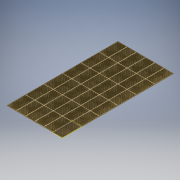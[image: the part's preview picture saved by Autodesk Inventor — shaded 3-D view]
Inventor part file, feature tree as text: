
AUTODESK INVENTOR PART (.ipt)
format: ipt  version: 2018 (Build 220112000, 112)  size: 17,295,360 bytes
history: native  units: in
note: dims shown in document units (in); Inventor stores cm internally (conversion verified against a paired STEP export)
features: extrude x2, sketch x2, plane x1, pattern_linear x1
ambient origin geometry x8: Origin, YZ Plane, XZ Plane, XY Plane, X Axis, Y Axis, Z Axis, Center Point
bodies: Solid1 (feature_tree)
feature tree (6):
  extrude  "Extrusion1"  Depth=240.0in
  extrude  "Extrusion2"  Depth=10.0in
  plane  "Work Plane1"
  pattern_linear  "Rectangular Pattern1"  Spacing1=10.0in  [1 undecoded]
  sketch  "Sketch1"  dims[d0=120.0in d1=240.0in]
  sketch  "Sketch2"  dims[d2=7.0in d3=0.0in d4=10.0in d5=10.0in d6=8.2677in d8=11.0in d9=3.937in d11=11.0in d14=1.0in d15=0.0in d16=90.0deg d17=2.3622in d19=120.0in d29=2.3622in d31=240.0in]
note: 1 required parameter value undecoded (feature->parameter linkage not recoverable at this tier; creation-order binding heuristic only, values carry confidence <= 0.55)
